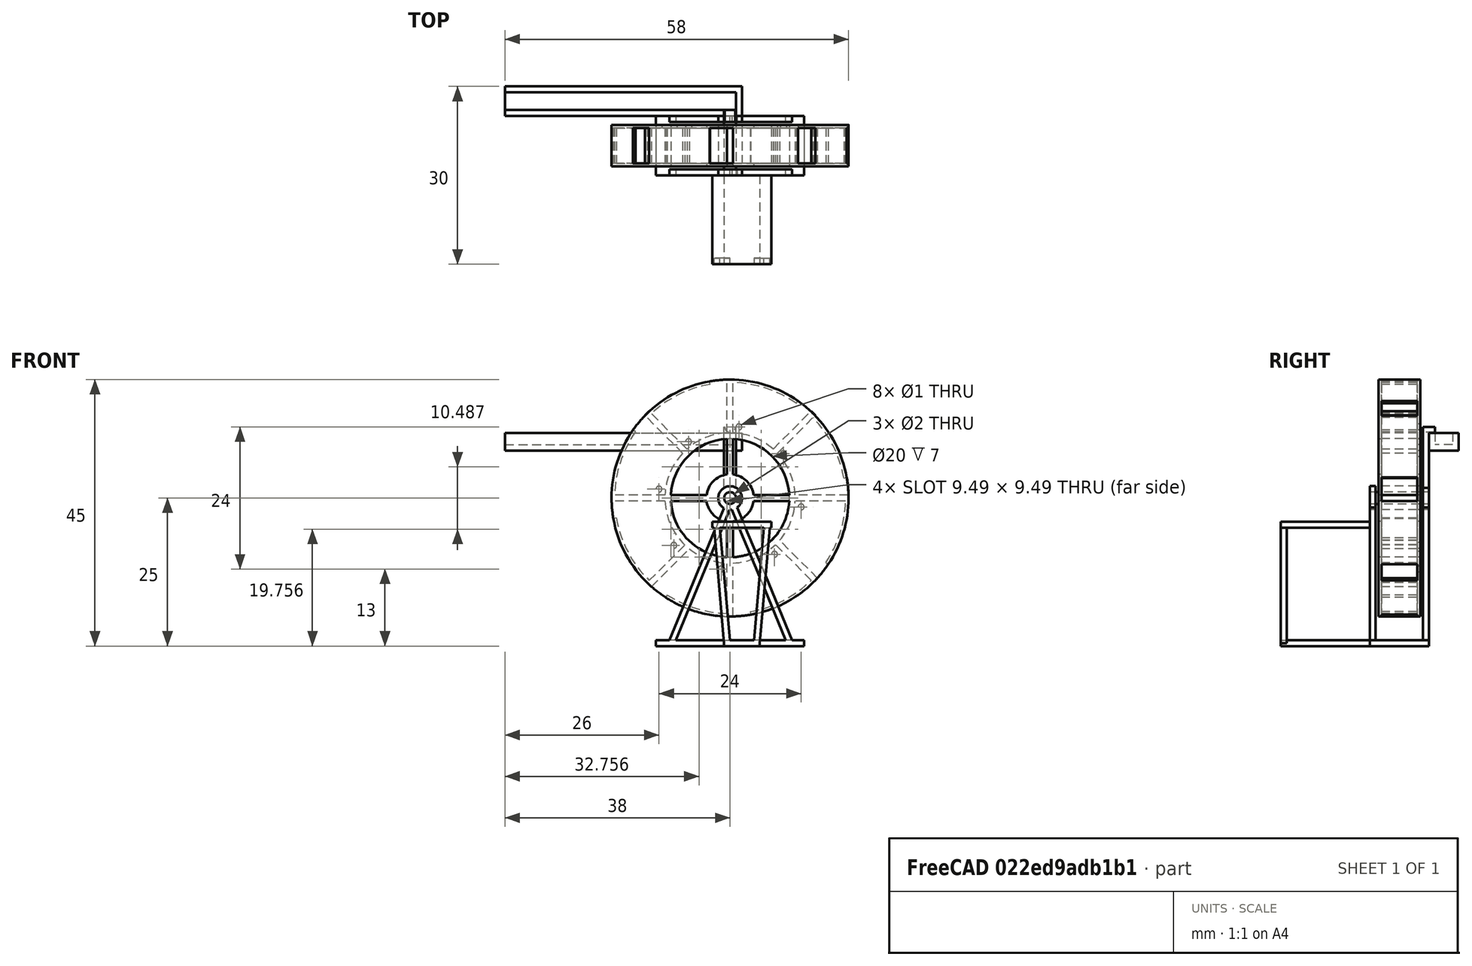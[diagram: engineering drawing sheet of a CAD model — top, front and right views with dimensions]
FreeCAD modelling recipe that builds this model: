
FCSTD DOCUMENT  (FreeCAD 0.18R4 (GitTag))
Label: BASE NORIA
License: All rights reserved
LicenseURL: http://en.wikipedia.org/wiki/All_rights_reserved
objects: Part::Cylinder×35, Part::Box×27, Part::Cut×25, Part::MultiFuse×10
note: 97 computed .brp shape members not serialized (recipe doc carries the construction recipe); baked Part::Feature solids carry a one-line shape summary decoded from their .brp

FEATURE [Part::Cylinder] Cylinder007  label="EJE"
  Angle = 360
  AttacherType = Attacher::AttachEngine3D
  Height = 10
  Placement = pos=(0,2,25) rot=(1,0,0;1.5708rad)
  Radius = 1
FEATURE [Part::Cylinder] Cylinder013  label="Cilindro013"
  Angle = 360
  AttacherType = Attacher::AttachEngine3D
  Height = 1
  Placement = pos=(0,0,6.5) rot=(0,0,1;0rad)
  Radius = 1
FEATURE [Part::Cylinder] Cylinder014  label="Cilindro014"
  Angle = 360
  AttacherType = Attacher::AttachEngine3D
  Height = 1
  Placement = pos=(0,0,6.5) rot=(0,0,1;0rad)
  Radius = 2
FEATURE [Part::Cut] Cut004
  Base = -> Cylinder014
  Placement = pos=(0,0,-8.5) rot=(0,0,1;0rad)
  Refine = true
  Tool = -> Cylinder013
FEATURE [Part::Box] Box  label="Cubo015"
  AttacherType = Attacher::AttachEngine3D
  Height = 25
  Length = 1
  Placement = pos=(-0.5,-1.5,-2) rot=(1,0,0;1.5708rad)
  Width = 1
FEATURE [Part::Box] Box017  label="Cubo016"
  AttacherType = Attacher::AttachEngine3D
  Height = 1
  Length = 1
  Placement = pos=(-0.5,-1.5,-2) rot=(0,0,1;2.35619rad)
  Width = 25
FEATURE [Part::MultiFuse] Fusion008  label="PARAL1"
  Placement = pos=(0,25,0) rot=(0,0,1;0.392699rad)
  Refine = true
  Shapes = -> [Cut004,Box017,Box]
FEATURE [Part::Box] Box018  label="Cubo017"
  AttacherType = Attacher::AttachEngine3D
  Height = 25
  Length = 1
  Placement = pos=(-0.5,-1.5,-2) rot=(1,0,0;1.5708rad)
  Width = 1
FEATURE [Part::Cylinder] Cylinder015  label="Cilindro015"
  Angle = 360
  AttacherType = Attacher::AttachEngine3D
  Height = 1
  Placement = pos=(0,0,6.5) rot=(0,0,1;0rad)
  Radius = 2
FEATURE [Part::Box] Box019  label="Cubo018"
  AttacherType = Attacher::AttachEngine3D
  Height = 1
  Length = 1
  Placement = pos=(-0.5,-1.5,-2) rot=(0,0,1;2.35619rad)
  Width = 25
FEATURE [Part::Cylinder] Cylinder016  label="Cilindro016"
  Angle = 360
  AttacherType = Attacher::AttachEngine3D
  Height = 1
  Placement = pos=(0,0,6.5) rot=(0,0,1;0rad)
  Radius = 1
FEATURE [Part::Cut] Cut005
  Base = -> Cylinder015
  Placement = pos=(0,0,-8.5) rot=(0,0,1;0rad)
  Refine = true
  Tool = -> Cylinder016
FEATURE [Part::MultiFuse] Fusion009  label="PARAL2"
  Placement = pos=(0,25,9) rot=(0,0,1;0.392699rad)
  Refine = true
  Shapes = -> [Cut005,Box019,Box018]
FEATURE [Part::Box] Box020  label="BASE"
  AttacherType = Attacher::AttachEngine3D
  Height = 10
  Length = 25
  Placement = pos=(-12.5,0,-2) rot=(0,0,1;0rad)
  Width = 1
FEATURE [Part::Box] Box010  label="Cubo009"
  AttacherType = Attacher::AttachEngine3D
  Height = 6
  Length = 1
  Placement = pos=(-7.31178,6.87403,0) rot=(0,0,1;0.785398rad)
  Width = 10
FEATURE [Part::Box] Box008  label="Cubo004"
  AttacherType = Attacher::AttachEngine3D
  Height = 0.5
  Length = 20
  Placement = pos=(0.5,-10,0) rot=(0,0,1;1.5708rad)
  Width = 1
FEATURE [Part::Cylinder] Cylinder005  label="Cilindro005"
  Angle = 360
  AttacherType = Attacher::AttachEngine3D
  Height = 0.5
  Radius = 10
FEATURE [Part::Box] Box009  label="Cubo005"
  AttacherType = Attacher::AttachEngine3D
  Height = 0.5
  Length = 20
  Placement = pos=(-10,-0.5,0) rot=(0,0,1;0rad)
  Width = 1
FEATURE [Part::Box] Box001  label="Cubo003"
  AttacherType = Attacher::AttachEngine3D
  Height = 0.5
  Length = 20
  Placement = pos=(0.5,-10,0) rot=(0,0,1;1.5708rad)
  Width = 1
FEATURE [Part::Cylinder] Cylinder004  label="Cilindro004"
  Angle = 360
  AttacherType = Attacher::AttachEngine3D
  Height = 0.5
  Radius = 4
FEATURE [Part::Cylinder] Cylinder003  label="Cilindro003"
  Angle = 360
  AttacherType = Attacher::AttachEngine3D
  Height = 0.5
  Radius = 10
FEATURE [Part::Cylinder] Cylinder  label="Cilindro"
  Angle = 360
  AttacherType = Attacher::AttachEngine3D
  Height = 7
  Radius = 20
FEATURE [Part::Cylinder] Cylinder001  label="Cilindro001"
  Angle = 360
  AttacherType = Attacher::AttachEngine3D
  Height = 7
  Radius = 19.5
FEATURE [Part::Cut] Cut
  Base = -> Cylinder
  Placement = pos=(0,0,-0.5) rot=(0,0,1;0rad)
  Refine = true
  Tool = -> Cylinder001
FEATURE [Part::Box] Box004  label="Cubo011"
  AttacherType = Attacher::AttachEngine3D
  Height = 6
  Length = 1
  Placement = pos=(-0.5,10,0) rot=(0,0,1;0rad)
  Width = 10
FEATURE [Part::Cylinder] Cylinder006  label="Cilindro006"
  Angle = 360
  AttacherType = Attacher::AttachEngine3D
  Height = 0.5
  Radius = 20
FEATURE [Part::Cut] Cut001
  Base = -> Cylinder006
  Refine = true
  Tool = -> Cylinder005
FEATURE [Part::Cylinder] Cylinder002  label="Cilindro002"
  Angle = 360
  AttacherType = Attacher::AttachEngine3D
  Height = 0.5
  Radius = 4
FEATURE [Part::Cylinder] Cylinder008  label="Cilindro008"
  Angle = 360
  AttacherType = Attacher::AttachEngine3D
  Height = 6
  Radius = 10
FEATURE [Part::Box] Box012  label="Cubo006"
  AttacherType = Attacher::AttachEngine3D
  Height = 6
  Length = 1
  Placement = pos=(-10,-0.5,0) rot=(0,0,1;1.5708rad)
  Width = 10
FEATURE [Part::Box] Box014  label="Cubo012"
  AttacherType = Attacher::AttachEngine3D
  Height = 6
  Length = 1
  Placement = pos=(14.04,-14.23,0) rot=(0,0,1;0.785398rad)
  Width = 10
FEATURE [Part::Box] Box015  label="Cubo013"
  AttacherType = Attacher::AttachEngine3D
  Height = 6
  Length = 1
  Placement = pos=(-14,-14.3,0) rot=(0,0,-1;0.785398rad)
  Width = 10
FEATURE [Part::Box] Box013  label="Cubo007"
  AttacherType = Attacher::AttachEngine3D
  Height = 6
  Length = 1
  Placement = pos=(20,-0.5,0) rot=(0,0,1;1.5708rad)
  Width = 10
FEATURE [Part::Cylinder] Cylinder009  label="Cilindro009"
  Angle = 360
  AttacherType = Attacher::AttachEngine3D
  Height = 6
  Radius = 11
FEATURE [Part::Cut] Cut003
  Base = -> Cylinder009
  Refine = true
  Tool = -> Cylinder008
FEATURE [Part::Box] Box011  label="Cubo010"
  AttacherType = Attacher::AttachEngine3D
  Height = 6
  Length = 1
  Placement = pos=(-0.5,-20,0) rot=(0,0,1;0rad)
  Width = 10
FEATURE [Part::Box] Box016  label="Cubo014"
  AttacherType = Attacher::AttachEngine3D
  Height = 6
  Length = 1
  Placement = pos=(6.6002,7.59413,0) rot=(0,0,-1;0.785398rad)
  Width = 10
FEATURE [Part::Box] Box007  label="Cubo"
  AttacherType = Attacher::AttachEngine3D
  Height = 0.5
  Length = 20
  Placement = pos=(-10,-0.5,0) rot=(0,0,1;0rad)
  Width = 1
FEATURE [Part::MultiFuse] Fusion007
  Placement = pos=(0,0,-0.5) rot=(0,0,1;0rad)
  Refine = true
  Shapes = -> [Cylinder002,Cut001,Box007,Box001]
FEATURE [Part::Cylinder] Cylinder010  label="Cilindro010"
  Angle = 360
  AttacherType = Attacher::AttachEngine3D
  Height = 0.5
  Radius = 20
FEATURE [Part::Cut] Cut002
  Base = -> Cylinder010
  Refine = true
  Tool = -> Cylinder003
FEATURE [Part::MultiFuse] Fusion006
  Placement = pos=(0,0,6) rot=(0,0,1;0rad)
  Refine = true
  Shapes = -> [Box008,Cut002,Box009,Cylinder004]
FEATURE [Part::MultiFuse] Fusion  label="NORIA"
  Refine = true
  Shapes = -> [Fusion006,Cut003,Box010,Box004,Box011,Box014,Box013,Box012,Box015,Box016,Fusion007]
FEATURE [Part::Cylinder] Cylinder017  label="Cilindro017"
  Angle = 10
  AttacherType = Attacher::AttachEngine3D
  Height = 7
  Placement = pos=(0,0,-0.5) rot=(0,0,-1;1.5708rad)
  Radius = 20
FEATURE [Part::Cylinder] Cylinder022  label="Cilindro022"
  Angle = 360
  AttacherType = Attacher::AttachEngine3D
  Height = 1
  Placement = pos=(12,-1.5,-1) rot=(0,0,1;0rad)
  Radius = 0.5
FEATURE [Part::Cylinder] Cylinder011  label="Cilindro011"
  Angle = 10
  AttacherType = Attacher::AttachEngine3D
  Height = 7
  Placement = pos=(0,0,-0.5) rot=(0,0,1;0rad)
  Radius = 20
FEATURE [Part::Cut] Cut021
  Base = -> Cut
  Refine = true
  Tool = -> Cylinder011
FEATURE [Part::Cylinder] Cylinder024  label="Cilindro024"
  Angle = 360
  AttacherType = Attacher::AttachEngine3D
  Height = 1
  Placement = pos=(-1.5,-12,-1) rot=(0,0,1;0rad)
  Radius = 0.5
FEATURE [Part::Cylinder] Cylinder025  label="Cilindro025"
  Angle = 10
  AttacherType = Attacher::AttachEngine3D
  Height = 7
  Placement = pos=(0,0,-0.5) rot=(0,0,1;2.35619rad)
  Radius = 20
FEATURE [Part::Cylinder] Cylinder018  label="Cilindro018"
  Angle = 10
  AttacherType = Attacher::AttachEngine3D
  Height = 7
  Placement = pos=(0,0,-0.5) rot=(0,0,-1;0.767945rad)
  Radius = 20
FEATURE [Part::Cylinder] Cylinder020  label="Cilindro020"
  Angle = 360
  AttacherType = Attacher::AttachEngine3D
  Height = 1
  Placement = pos=(7.5,-9.5,-1) rot=(0,0,1;0rad)
  Radius = 0.5
FEATURE [Part::Cylinder] Cylinder021  label="Cilindro021"
  Angle = 360
  AttacherType = Attacher::AttachEngine3D
  Height = 1
  Placement = pos=(1.5,12,-1) rot=(0,0,1;0rad)
  Radius = 0.5
FEATURE [Part::Cylinder] Cylinder026  label="Cilindro026"
  Angle = 10
  AttacherType = Attacher::AttachEngine3D
  Height = 7
  Placement = pos=(0,0,-0.5) rot=(0,0,1;1.5708rad)
  Radius = 20
FEATURE [Part::Cylinder] Cylinder012  label="Cilindro012"
  Angle = 10
  AttacherType = Attacher::AttachEngine3D
  Height = 7
  Placement = pos=(0,0,-0.5) rot=(0,0,1;0.785398rad)
  Radius = 20
FEATURE [Part::Cut] Cut022
  Base = -> Cut021
  Refine = true
  Tool = -> Cylinder012
FEATURE [Part::Cut] Cut006
  Base = -> Cut022
  Refine = true
  Tool = -> Cylinder025
FEATURE [Part::Cut] Cut007
  Base = -> Cut006
  Refine = true
  Tool = -> Cylinder026
FEATURE [Part::Cylinder] Cylinder027  label="Cilindro027"
  Angle = 10
  AttacherType = Attacher::AttachEngine3D
  Height = 7
  Placement = pos=(0,0,-0.5) rot=(0,0,1;3.9619rad)
  Radius = 20
FEATURE [Part::Cut] Cut008
  Base = -> Cut007
  Refine = true
  Tool = -> Cylinder027
FEATURE [Part::Cylinder] Cylinder028  label="Cilindro028"
  Angle = 10
  AttacherType = Attacher::AttachEngine3D
  Height = 7
  Placement = pos=(0,0,-0.5) rot=(0,0,1;3.14159rad)
  Radius = 20
FEATURE [Part::Cut] Cut009
  Base = -> Cut008
  Refine = true
  Tool = -> Cylinder028
FEATURE [Part::Cut] Cut010
  Base = -> Cut009
  Refine = true
  Tool = -> Cylinder017
FEATURE [Part::Cut] Cut011
  Base = -> Cut010
  Refine = true
  Tool = -> Cylinder018
FEATURE [Part::MultiFuse] Fusion010
  Refine = true
  Shapes = -> [Fusion,Cut011]
FEATURE [Part::Cylinder] Cylinder019  label="Cilindro019"
  Angle = 360
  AttacherType = Attacher::AttachEngine3D
  Height = 10
  Placement = pos=(0,0,-1) rot=(0,0,1;0rad)
  Radius = 1
FEATURE [Part::Cut] Cut012
  Base = -> Fusion010
  Refine = true
  Tool = -> Cylinder019
FEATURE [Part::Cut] Cut013
  Base = -> Cut012
  Refine = true
  Tool = -> Cylinder020
FEATURE [Part::Cut] Cut014
  Base = -> Cut013
  Refine = true
  Tool = -> Cylinder021
FEATURE [Part::Cut] Cut015
  Base = -> Cut014
  Refine = true
  Tool = -> Cylinder022
FEATURE [Part::Cylinder] Cylinder029  label="Cilindro029"
  Angle = 360
  AttacherType = Attacher::AttachEngine3D
  Height = 1
  Placement = pos=(-9.5,-8,-1) rot=(0,0,1;0rad)
  Radius = 0.5
FEATURE [Part::Cylinder] Cylinder030  label="Cilindro030"
  Angle = 360
  AttacherType = Attacher::AttachEngine3D
  Height = 1
  Placement = pos=(9,7.5,-1) rot=(0,0,1;0rad)
  Radius = 0.5
FEATURE [Part::Cylinder] Cylinder031  label="Cilindro031"
  Angle = 360
  AttacherType = Attacher::AttachEngine3D
  Height = 1
  Placement = pos=(-7,9.5,-1) rot=(0,0,1;0rad)
  Radius = 0.5
FEATURE [Part::Cylinder] Cylinder032  label="Cilindro032"
  Angle = 360
  AttacherType = Attacher::AttachEngine3D
  Height = 1
  Placement = pos=(-12,1.5,-1) rot=(0,0,1;0rad)
  Radius = 0.5
FEATURE [Part::Cut] Cut016
  Base = -> Cut015
  Refine = true
  Tool = -> Cylinder030
FEATURE [Part::Cut] Cut017
  Base = -> Cut016
  Refine = true
  Tool = -> Cylinder031
FEATURE [Part::Cut] Cut018
  Base = -> Cut017
  Refine = true
  Tool = -> Cylinder024
FEATURE [Part::Cut] Cut019
  Base = -> Cut018
  Refine = true
  Tool = -> Cylinder032
FEATURE [Part::Cut] Cut020  label="PARTE DE NORIA"
  Base = -> Cut019
  Placement = pos=(0,0,25) rot=(1,0,0;1.5708rad)
  Refine = true
  Tool = -> Cylinder029
FEATURE [Part::Box] Box021  label="Cubo019"
  AttacherType = Attacher::AttachEngine3D
  Height = 15
  Length = 10
  Placement = pos=(-3,20,8) rot=(0,0,1;0rad)
  Width = 1
FEATURE [Part::Box] Box022  label="Cubo020"
  AttacherType = Attacher::AttachEngine3D
  Height = 15
  Length = 6
  Placement = pos=(-1,0,8) rot=(0,0,1;0rad)
  Width = 1
FEATURE [Part::MultiFuse] Fusion011  label="BASE DE NORIA"
  Refine = true
  Shapes = -> [Box022,Box020]
FEATURE [Part::Box] Box023  label="Cubo021"
  AttacherType = Attacher::AttachEngine3D
  Height = 5
  Length = 40
  Placement = pos=(-38,33,-7) rot=(0,0,1;0rad)
  Width = 1
FEATURE [Part::Box] Box024  label="Cubo022"
  AttacherType = Attacher::AttachEngine3D
  Height = 1
  Length = 2
  Placement = pos=(-1,26.5,-2) rot=(0,0,1;0rad)
  Width = 9.5
FEATURE [Part::Box] Box025  label="Cubo023"
  AttacherType = Attacher::AttachEngine3D
  Height = 2
  Length = 40
  Placement = pos=(-38,36,-7) rot=(1,0,0;1.5708rad)
  Width = 1
FEATURE [Part::Box] Box026  label="Cubo024"
  AttacherType = Attacher::AttachEngine3D
  Height = 2
  Length = 40
  Placement = pos=(-38,36,-3) rot=(1,0,0;1.5708rad)
  Width = 1
FEATURE [Part::Box] Box027  label="Cubo025"
  AttacherType = Attacher::AttachEngine3D
  Height = 1
  Length = 1
  Placement = pos=(4,0.5,22) rot=(0,0,1;-0.087266rad)
  Width = 20
FEATURE [Part::Box] Box028  label="Cubo026"
  AttacherType = Attacher::AttachEngine3D
  Height = 1
  Length = 1
  Placement = pos=(-1,0.5,22) rot=(0,0,1;0.087266rad)
  Width = 20
FEATURE [Part::Box] Box029  label="Cubo027"
  AttacherType = Attacher::AttachEngine3D
  Height = 3
  Length = 1
  Placement = pos=(1,34,-6) rot=(0,0,1;0rad)
  Width = 2
FEATURE [Part::MultiFuse] Fusion014  label="CANAL"
  Placement = pos=(0,0,0) rot=(1,0,0;1.5708rad)
  Refine = true
  Shapes = -> [Box029,Box023,Box025,Box026]
FEATURE [Part::Cylinder] Cylinder033  label="Cilindro033"
  Angle = 180
  AttacherType = Attacher::AttachEngine3D
  Height = 2
  Placement = pos=(0,37,-3) rot=(0,0,1;3.14159rad)
  Radius = 0.9
FEATURE [Part::Box] Box030  label="Cubo028"
  AttacherType = Attacher::AttachEngine3D
  Height = 2
  Length = 2
  Placement = pos=(-1,36,-3) rot=(0,0,1;0rad)
  Width = 1
FEATURE [Part::Cut] Cut023
  Base = -> Box030
  Refine = true
  Tool = -> Cylinder033
FEATURE [Part::MultiFuse] Fusion015  label="BASE NORIA"
  Placement = pos=(0,0,0) rot=(1,0,0;1.5708rad)
  Refine = true
  Shapes = -> [Cut023,Box024,Box021,Box027,Fusion011,Box028,Fusion008,Fusion009]
FEATURE [Part::Cylinder] Cylinder034  label="EJE001"
  Angle = 360
  AttacherType = Attacher::AttachEngine3D
  Height = 6
  Placement = pos=(0,0,25) rot=(1,0,0;1.5708rad)
  Radius = 2
FEATURE [Part::Cylinder] Cylinder035  label="EJE002"
  Angle = 360
  AttacherType = Attacher::AttachEngine3D
  Height = 6
  Placement = pos=(0,0,25) rot=(1,0,0;1.5708rad)
  Radius = 1
FEATURE [Part::Cut] Cut024  label="ARANDELA"
  Base = -> Cylinder034
  Refine = true
  Tool = -> Cylinder035
FEATURE [Part::MultiFuse] Fusion016  label="NORIA FINAL"
  Refine = true
  Shapes = -> [Cut024,Cut020]
